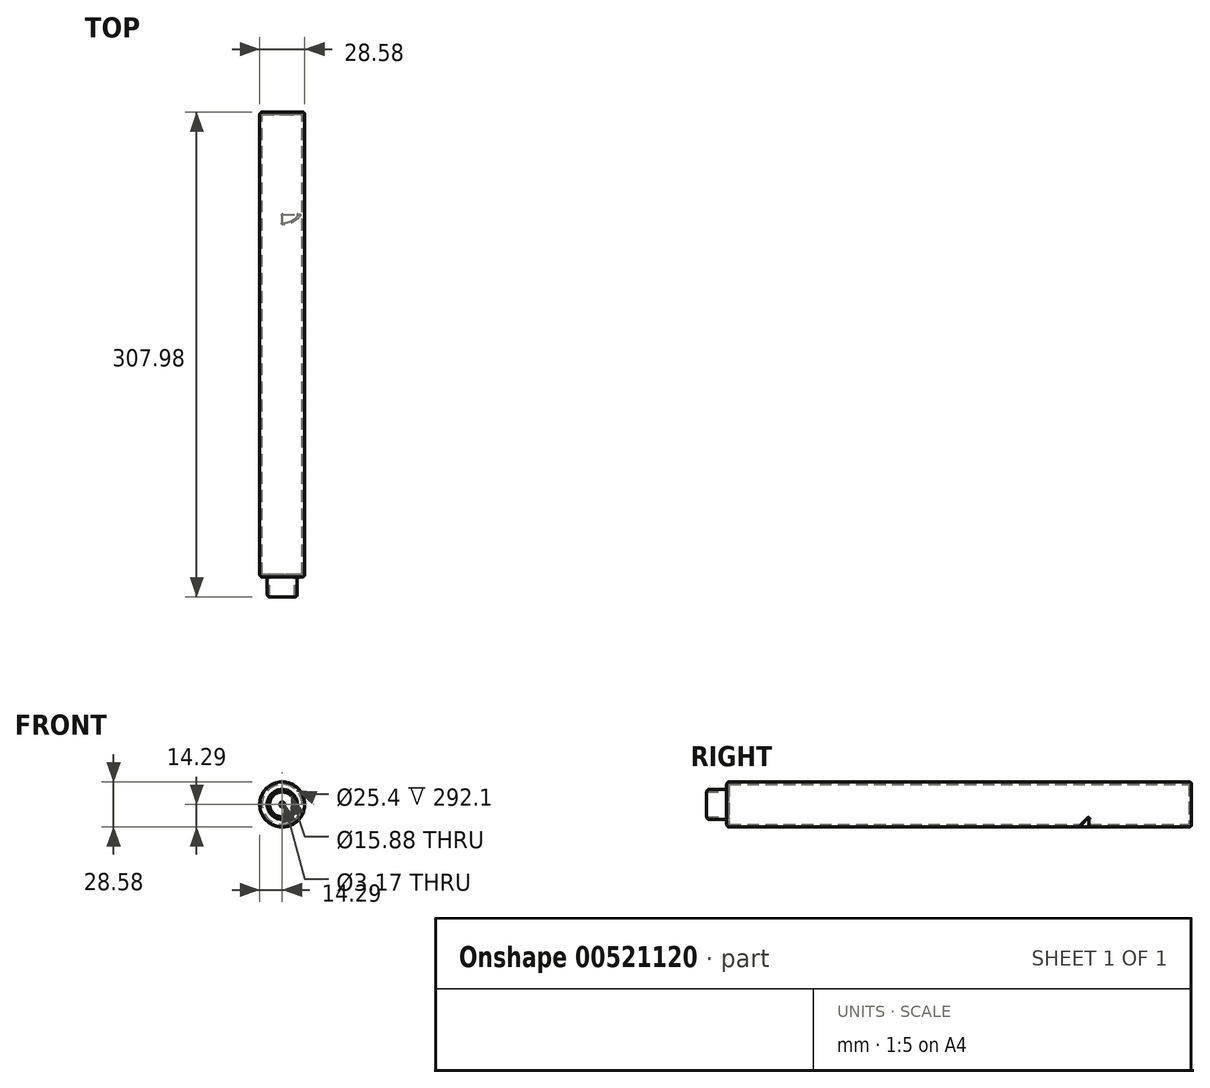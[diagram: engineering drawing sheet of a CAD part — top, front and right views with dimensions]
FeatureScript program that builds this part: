
annotation { "Feature Type Name" : "Feature", "Feature Type Description" : "" }
export const myFeature = defineFeature(function(context is Context, id is Id, definition is map)
    precondition{}
    {
        {
            var Q0;
            Q0=qCreatedBy(makeId("Right.planeOp"),FACE);
            var sketch = newSketch(context, id + "F0", { "sketchPlane" : qUnion([Q0])});
            skLineSegment(sketch, "E0.bottom", {"start": v(-139.7, 14.29) * mm, "end": v(152.4, 14.29) * mm});
            skLineSegment(sketch, "E0.top", {"start": v(-139.7, 12.7) * mm, "end": v(152.4, 12.7) * mm});
            skLineSegment(sketch, "E1.bottom", {"start": v(-141.29, 9.52) * mm, "end": v(-153.99, 9.52) * mm});
            skLineSegment(sketch, "E1.top", {"start": v(-141.29, 7.94) * mm, "end": v(-153.99, 7.94) * mm});
            skLineSegment(sketch, "E1.right", {"start": v(-153.99, 9.52) * mm, "end": v(-153.99, 7.94) * mm});
            skLineSegment(sketch, "E2.bottom", {"start": v(-139.7, 14.29) * mm, "end": v(-141.29, 14.29) * mm});
            skLineSegment(sketch, "E2.top", {"start": v(-139.7, 7.94) * mm, "end": v(-141.29, 7.94) * mm});
            skLineSegment(sketch, "E2.left", {"start": v(-139.7, 12.7) * mm, "end": v(-139.7, 7.94) * mm});
            skLineSegment(sketch, "E2.right", {"start": v(-141.29, 14.29) * mm, "end": v(-141.29, 9.52) * mm});
            skLineSegment(sketch, "E3.bottom", {"start": v(152.4, 14.29) * mm, "end": v(153.99, 14.29) * mm});
            skLineSegment(sketch, "E3.top", {"start": v(152.4, 1.59) * mm, "end": v(153.99, 1.59) * mm});
            skLineSegment(sketch, "E3.left", {"start": v(152.4, 12.7) * mm, "end": v(152.4, 1.59) * mm});
            skLineSegment(sketch, "E3.right", {"start": v(153.99, 14.29) * mm, "end": v(153.99, 1.59) * mm});
            skLineSegment(sketch, "E4", {"start": v(0, 0) * mm, "end": v(-28.81, 0) * mm, "construction": true});
            skSolve(sketch);
        }
        {
            var Q0;
            Q0=makeQuery(id+"F0.imprint","IMPRINT",FACE,{"disambiguationData":[TD([[makeQuery(id+"F0.imprint","IMPRINT",EDGE,{"derivedFrom":sQuery(id+"F0.wireOp",EDGE,"E0.bottom")}),-1.0]])]});
            var Q1;
            Q1=sQuery(id+"F0.wireOp",EDGE,"E4");
            revolve(context, id + "F1", {"entities" : qUnion([Q0]), "axis" : qUnion([Q1]), "revolveType" : RevolveType.FULL});
        }
        {
            var Q0;
            Q0=makeQuery(id+"F1.opRevolve","SWEPT_EDGE",EDGE,{"disambiguationData":[OSD([sQuery(id+"F0.wireOp",EDGE,"E2.bottom"),sQuery(id+"F0.wireOp",EDGE,"E2.right")])]});
            var Q1;
            Q1=makeQuery(id+"F1.opRevolve","SWEPT_EDGE",EDGE,{"disambiguationData":[OSD([sQuery(id+"F0.wireOp",EDGE,"E1.bottom"),sQuery(id+"F0.wireOp",EDGE,"E2.right")])]});
            var Q2;
            Q2=makeQuery(id+"F1.opRevolve","SWEPT_EDGE",EDGE,{"disambiguationData":[OSD([sQuery(id+"F0.wireOp",EDGE,"E1.bottom"),sQuery(id+"F0.wireOp",EDGE,"E1.right")])]});
            var Q3;
            Q3=makeQuery(id+"F1.opRevolve","SWEPT_EDGE",EDGE,{"disambiguationData":[OSD([sQuery(id+"F0.wireOp",EDGE,"E3.bottom"),sQuery(id+"F0.wireOp",EDGE,"E3.right")])]});
            var Q4;
            Q4=makeQuery(id+"F1.opRevolve","SWEPT_EDGE",EDGE,{"disambiguationData":[OSD([sQuery(id+"F0.wireOp",EDGE,"E2.top"),sQuery(id+"F0.wireOp",EDGE,"E2.left")])]});
            fillet(context, id + "F2", {"entities" : qUnion([Q0, Q1, Q2, Q3, Q4]), "radius" : 1.59 * mm, "tangentPropagation" : true, "allowEdgeOverflow" : false});
        }
        {
            var Q0;
            Q0=qCreatedBy(makeId("Right.planeOp"),FACE);
            var sketch = newSketch(context, id + "F3", { "sketchPlane" : qUnion([Q0])});
            skLineSegment(sketch, "E5.bottom", {"start": v(88.89, -14.29) * mm, "end": v(82.54, -14.29) * mm});
            skLineSegment(sketch, "E5.top", {"start": v(88.89, -7.94) * mm, "end": v(82.54, -7.94) * mm, "construction": true});
            skLineSegment(sketch, "E5.left", {"start": v(88.89, -14.29) * mm, "end": v(88.89, -7.94) * mm});
            skLineSegment(sketch, "E5.right", {"start": v(82.54, -14.29) * mm, "end": v(82.54, -7.94) * mm, "construction": true});
            skLineSegment(sketch, "E6", {"start": v(82.54, -14.29) * mm, "end": v(88.89, -7.94) * mm});
            skSolve(sketch);
        }
        {
            var Q0;
            Q0 = qSketchRegion(id + "F3", true);
            extrude(context, id + "F4", {"entities" : qUnion([Q0]), "operationType" : NewBodyOperationType.REMOVE, "depth" : 57.63 * mm, "offsetDistance" : 25.4 * mm});
        }
        {
            var Q0;
            Q0=makeQuery(id+"F4.boolean.opBoolean","COPY",FACE,{"derivedFrom":makeQuery(id+"F4.opExtrude","CAP_FACE",FACE,{"disambiguationData":[OSD([sQuery(id+"F3.wireOp",EDGE,"E5.bottom"),sQuery(id+"F3.wireOp",EDGE,"E5.left"),sQuery(id+"F3.wireOp",EDGE,"E6")])],"isStart":true})});
            var Q1;
            Q1=makeQuery(id+"F4.boolean.opBoolean","COPY",FACE,{"derivedFrom":makeQuery(id+"F4.opExtrude","SWEPT_FACE",FACE,{"disambiguationData":[OSD([sQuery(id+"F3.wireOp",EDGE,"E5.left")])]})});
            var Q2;
            Q2=makeQuery(id+"F4.boolean.opBoolean","COPY",FACE,{"derivedFrom":makeQuery(id+"F4.opExtrude","SWEPT_FACE",FACE,{"disambiguationData":[OSD([sQuery(id+"F3.wireOp",EDGE,"E6")])]})});
            fillet(context, id + "F5", {"entities" : qUnion([Q0, Q1, Q2]), "radius" : 0.4 * mm, "tangentPropagation" : true, "allowEdgeOverflow" : false});
        }
    });
